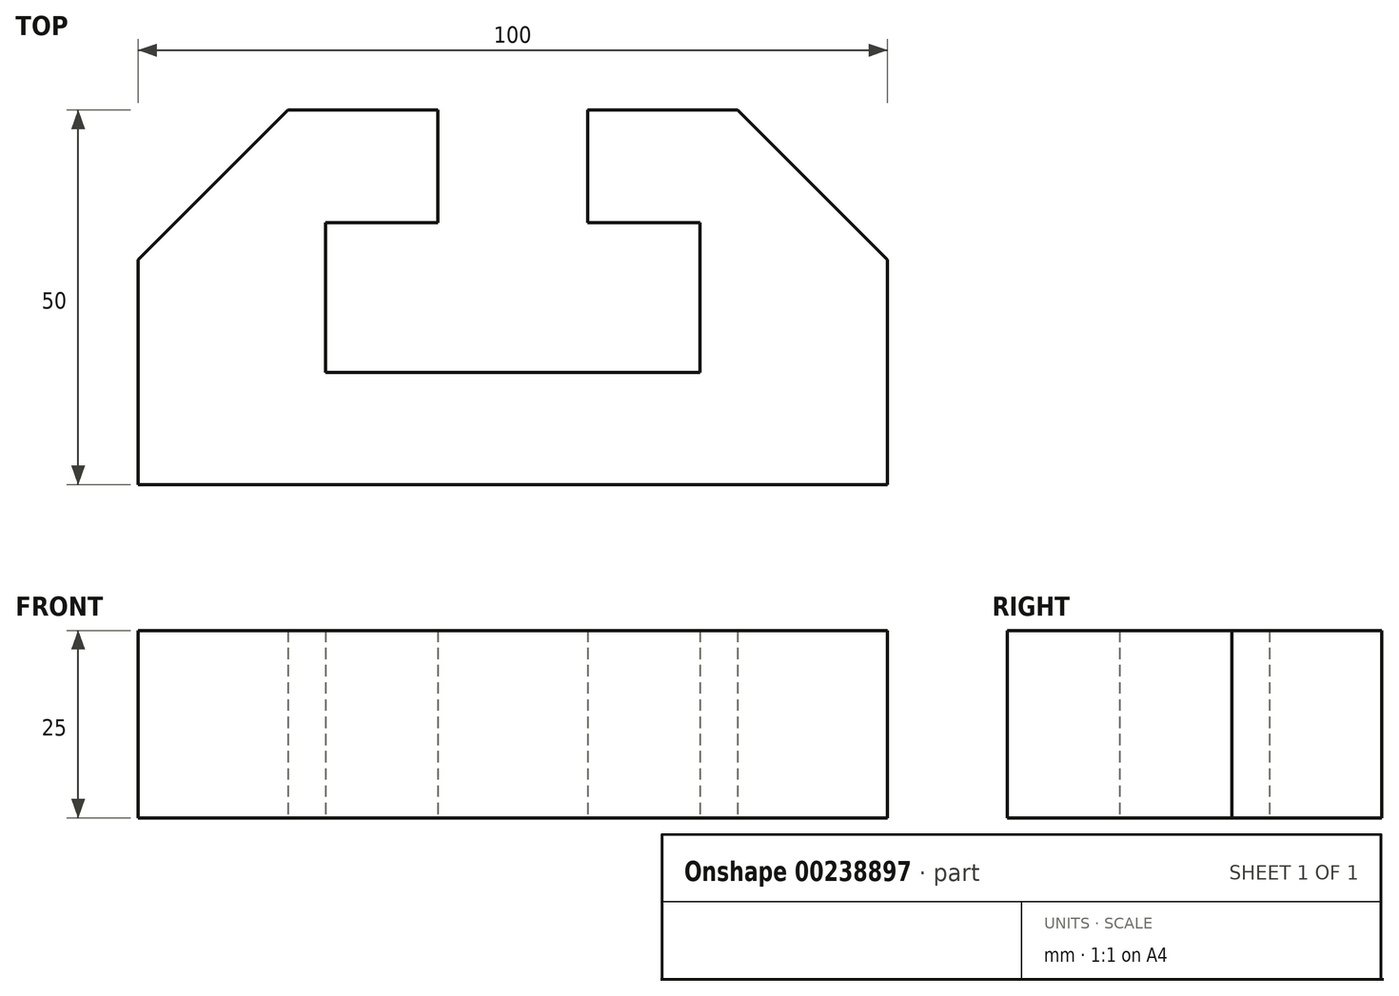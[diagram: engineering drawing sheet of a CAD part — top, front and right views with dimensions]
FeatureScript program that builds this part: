
annotation { "Feature Type Name" : "Feature", "Feature Type Description" : "" }
export const myFeature = defineFeature(function(context is Context, id is Id, definition is map)
    precondition{}
    {
        {
            var Q0;
            Q0=qCreatedBy(makeId("Top.planeOp"),FACE);
            var sketch = newSketch(context, id + "F0", { "sketchPlane" : qUnion([Q0])});
            skLineSegment(sketch, "E0", {"start": v(-53.39, -35) * mm, "end": v(46.61, -35) * mm});
            skLineSegment(sketch, "E1", {"start": v(-53.39, -35) * mm, "end": v(-53.39, -5) * mm});
            skLineSegment(sketch, "E2", {"start": v(-53.39, -5) * mm, "end": v(-33.39, 15) * mm});
            skLineSegment(sketch, "E3", {"start": v(46.61, -35) * mm, "end": v(46.61, -5) * mm});
            skLineSegment(sketch, "E4", {"start": v(46.61, -5) * mm, "end": v(26.61, 15) * mm});
            skLineSegment(sketch, "E5", {"start": v(-33.39, 15) * mm, "end": v(-13.39, 15) * mm});
            skLineSegment(sketch, "E6", {"start": v(26.61, 15) * mm, "end": v(6.61, 15) * mm});
            skLineSegment(sketch, "E7", {"start": v(-13.39, 15) * mm, "end": v(-13.39, 0) * mm});
            skLineSegment(sketch, "E8", {"start": v(6.61, 15) * mm, "end": v(6.61, 0) * mm});
            skLineSegment(sketch, "E9", {"start": v(-13.39, 0) * mm, "end": v(-28.39, 0) * mm});
            skLineSegment(sketch, "E10", {"start": v(6.61, 0) * mm, "end": v(21.61, 0) * mm});
            skLineSegment(sketch, "E11", {"start": v(-28.39, 0) * mm, "end": v(-28.39, -20) * mm});
            skLineSegment(sketch, "E12", {"start": v(21.61, 0) * mm, "end": v(21.61, -20) * mm});
            skLineSegment(sketch, "E13", {"start": v(-28.39, -20) * mm, "end": v(21.61, -20) * mm});
            skSolve(sketch);
        }
        {
            var Q0;
            Q0=makeQuery(id+"F0.imprint","IMPRINT",FACE,{"disambiguationData":[TD([[makeQuery(id+"F0.imprint","IMPRINT",EDGE,{"derivedFrom":sQuery(id+"F0.wireOp",EDGE,"E0")}),1.0]])]});
            extrude(context, id + "F1", {"entities" : qUnion([Q0]), "depth" : 25 * mm});
        }
    });
